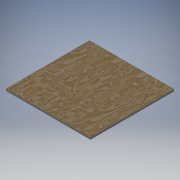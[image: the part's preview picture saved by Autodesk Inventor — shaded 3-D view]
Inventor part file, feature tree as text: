
AUTODESK INVENTOR PART (.ipt)
format: ipt  version: 2018.2 (Build 222227000, 227)  size: 111,616 bytes
history: native  units: in
note: dims shown in document units (in); Inventor stores cm internally (conversion verified against a paired STEP export)
features: extrude x1, sketch x1
ambient origin geometry x8: Origin, YZ Plane, XZ Plane, XY Plane, X Axis, Y Axis, Z Axis, Center Point
bodies: Solid1 (feature_tree)
feature tree (2):
  extrude  "Extrusion1"  Depth=30.898in
  sketch  "Sketch1"  dims[d0=31.225in d1=30.898in d2=0.75in d3=0.0in]
